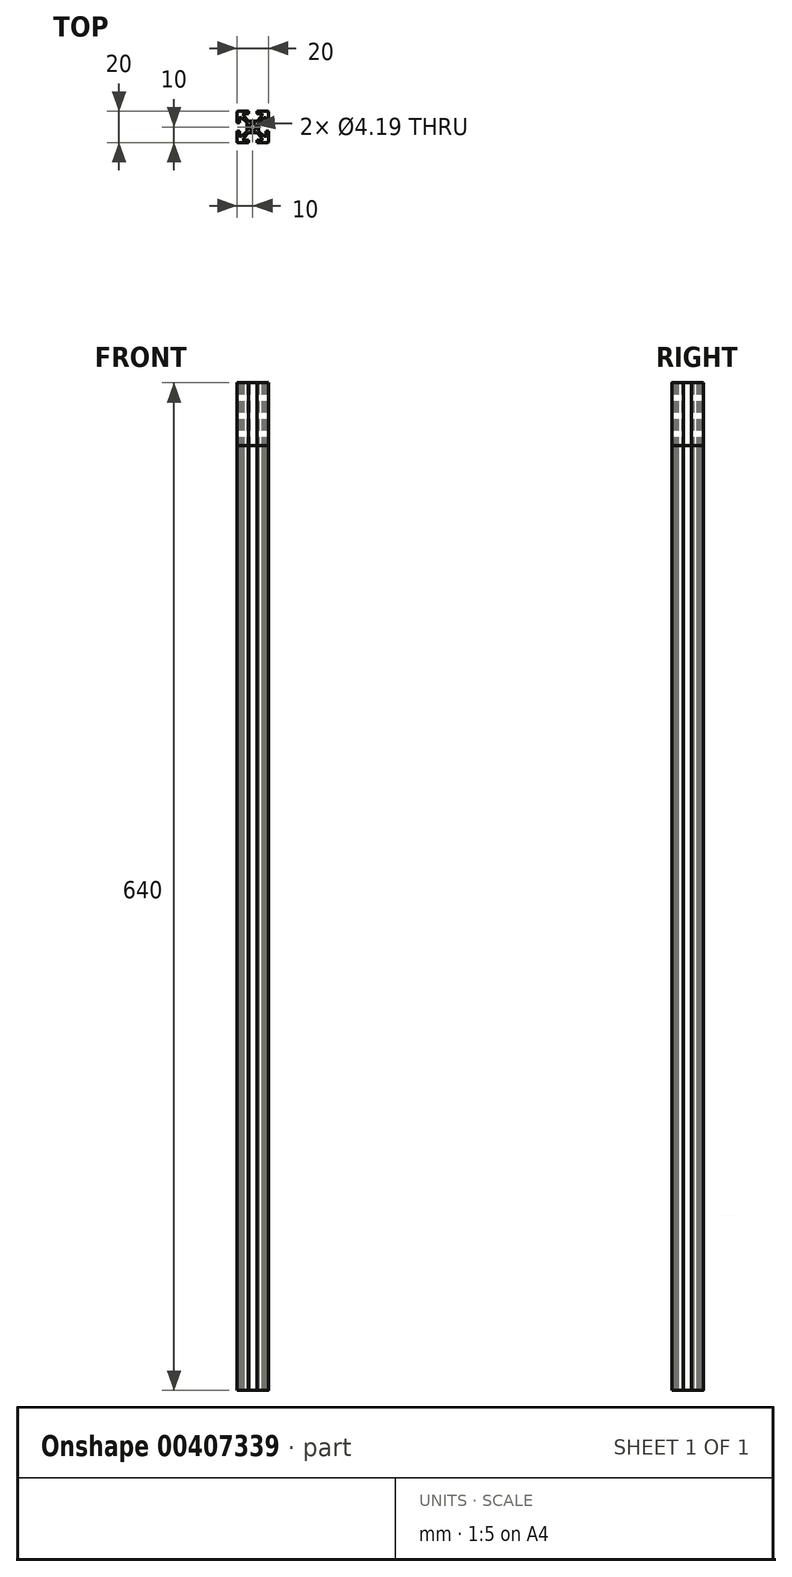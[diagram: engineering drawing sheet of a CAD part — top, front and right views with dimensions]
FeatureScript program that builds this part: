
annotation { "Feature Type Name" : "Feature", "Feature Type Description" : "" }
export const myFeature = defineFeature(function(context is Context, id is Id, definition is map)
    precondition{}
    {
        {
            var Q0;
            Q0=qCreatedBy(makeId("Top.planeOp"),FACE);
            var sketch = newSketch(context, id + "F0", { "sketchPlane" : qUnion([Q0])});
            skLineSegment(sketch, "E0", {"start": v(0, 3.66) * mm, "end": v(2.6, 3.66) * mm});
            skLineSegment(sketch, "E1", {"start": v(2.6, 3.66) * mm, "end": v(6, 7.06) * mm});
            skLineSegment(sketch, "E2", {"start": v(6, 7.06) * mm, "end": v(6, 7.86) * mm});
            skLineSegment(sketch, "E3", {"start": v(5.5, 8.36) * mm, "end": v(3.13, 8.36) * mm});
            skLineSegment(sketch, "E4", {"start": v(2.63, 8.86) * mm, "end": v(2.63, 9.5) * mm});
            skLineSegment(sketch, "E5", {"start": v(3.13, 10) * mm, "end": v(9.5, 10) * mm});
            skLineSegment(sketch, "E6", {"start": v(10, 9.5) * mm, "end": v(10, 3.13) * mm});
            skLineSegment(sketch, "E7", {"start": v(9.5, 2.63) * mm, "end": v(8.86, 2.63) * mm});
            skLineSegment(sketch, "E8", {"start": v(8.36, 3.13) * mm, "end": v(8.36, 5.5) * mm});
            skLineSegment(sketch, "E9", {"start": v(7.86, 6) * mm, "end": v(7.06, 6) * mm});
            skLineSegment(sketch, "E10", {"start": v(7.06, 6) * mm, "end": v(3.66, 2.6) * mm});
            skLineSegment(sketch, "E11", {"start": v(3.66, 2.6) * mm, "end": v(3.66, 0) * mm});
            skArc(sketch, "E12", {"start": v(2.1, 0) * mm, "mid": v(1.48, 1.48) * mm, "end": v(0, 2.1) * mm});
            skPoint(sketch, "E13.visualSharp", {"position": v(2.63, 10) * mm});
            skArc(sketch, "E13.filletArc", {"start": v(3.13, 10) * mm, "mid": v(2.78, 9.85) * mm, "end": v(2.63, 9.5) * mm});
            skPoint(sketch, "E14.visualSharp", {"position": v(2.63, 8.36) * mm});
            skArc(sketch, "E14.filletArc", {"start": v(2.63, 8.86) * mm, "mid": v(2.78, 8.5) * mm, "end": v(3.13, 8.36) * mm});
            skPoint(sketch, "E15.visualSharp", {"position": v(10, 10) * mm});
            skArc(sketch, "E15.filletArc", {"start": v(10, 9.5) * mm, "mid": v(9.85, 9.85) * mm, "end": v(9.5, 10) * mm});
            skPoint(sketch, "E16.visualSharp", {"position": v(10, 2.63) * mm});
            skArc(sketch, "E16.filletArc", {"start": v(9.5, 2.63) * mm, "mid": v(9.85, 2.78) * mm, "end": v(10, 3.13) * mm});
            skPoint(sketch, "E17.visualSharp", {"position": v(8.36, 6) * mm});
            skArc(sketch, "E17.filletArc", {"start": v(8.36, 5.5) * mm, "mid": v(8.21, 5.85) * mm, "end": v(7.86, 6) * mm});
            skPoint(sketch, "E18.visualSharp", {"position": v(8.36, 2.63) * mm});
            skArc(sketch, "E18.filletArc", {"start": v(8.36, 3.13) * mm, "mid": v(8.5, 2.78) * mm, "end": v(8.86, 2.63) * mm});
            skPoint(sketch, "E19.visualSharp", {"position": v(6, 8.36) * mm});
            skArc(sketch, "E19.filletArc", {"start": v(6, 7.86) * mm, "mid": v(5.85, 8.21) * mm, "end": v(5.5, 8.36) * mm});
            skLineSegment(sketch, "E20.MirrorCS", {"start": v(-2.63, 8.86) * mm, "end": v(-2.63, 9.5) * mm});
            skArc(sketch, "E21.MirrorCS", {"start": v(-8.36, 3.13) * mm, "mid": v(-8.5, 2.78) * mm, "end": v(-8.86, 2.63) * mm});
            skArc(sketch, "E22.MirrorCS", {"start": v(-6, 7.86) * mm, "mid": v(-5.85, 8.21) * mm, "end": v(-5.5, 8.36) * mm});
            skArc(sketch, "E23.MirrorCS", {"start": v(-3.13, 10) * mm, "mid": v(-2.78, 9.85) * mm, "end": v(-2.63, 9.5) * mm});
            skArc(sketch, "E24.MirrorCS", {"start": v(-2.63, 8.86) * mm, "mid": v(-2.78, 8.5) * mm, "end": v(-3.13, 8.36) * mm});
            skArc(sketch, "E25.MirrorCS", {"start": v(-10, 9.5) * mm, "mid": v(-9.85, 9.85) * mm, "end": v(-9.5, 10) * mm});
            skLineSegment(sketch, "E26.MirrorCS", {"start": v(-6, 7.06) * mm, "end": v(-6, 7.86) * mm});
            skLineSegment(sketch, "E27.MirrorCS", {"start": v(-9.5, 2.63) * mm, "end": v(-8.86, 2.63) * mm});
            skLineSegment(sketch, "E28.MirrorCS", {"start": v(-7.86, 6) * mm, "end": v(-7.06, 6) * mm});
            skArc(sketch, "E29.MirrorCS", {"start": v(-9.5, 2.63) * mm, "mid": v(-9.85, 2.78) * mm, "end": v(-10, 3.13) * mm});
            skArc(sketch, "E30.MirrorCS", {"start": v(-8.36, 5.5) * mm, "mid": v(-8.21, 5.85) * mm, "end": v(-7.86, 6) * mm});
            skPoint(sketch, "E31.MirrorP", {"position": v(-8.36, 2.63) * mm});
            skPoint(sketch, "E32.MirrorP", {"position": v(-10, 10) * mm});
            skPoint(sketch, "E33.MirrorP", {"position": v(-2.63, 8.36) * mm});
            skPoint(sketch, "E34.MirrorP", {"position": v(-6, 8.36) * mm});
            skPoint(sketch, "E35.MirrorP", {"position": v(-10, 2.63) * mm});
            skLineSegment(sketch, "E36.MirrorCS", {"start": v(0, 3.66) * mm, "end": v(-2.6, 3.66) * mm});
            skLineSegment(sketch, "E37.MirrorCS", {"start": v(-2.6, 3.66) * mm, "end": v(-6, 7.06) * mm});
            skLineSegment(sketch, "E38.MirrorCS", {"start": v(-5.5, 8.36) * mm, "end": v(-3.13, 8.36) * mm});
            skLineSegment(sketch, "E39.MirrorCS", {"start": v(-3.13, 10) * mm, "end": v(-9.5, 10) * mm});
            skLineSegment(sketch, "E40.MirrorCS", {"start": v(-10, 9.5) * mm, "end": v(-10, 3.13) * mm});
            skLineSegment(sketch, "E41.MirrorCS", {"start": v(-8.36, 3.13) * mm, "end": v(-8.36, 5.5) * mm});
            skLineSegment(sketch, "E42.MirrorCS", {"start": v(-3.66, 2.6) * mm, "end": v(-3.66, 0) * mm});
            skLineSegment(sketch, "E43.MirrorCS", {"start": v(-7.06, 6) * mm, "end": v(-3.66, 2.6) * mm});
            skArc(sketch, "E44.MirrorCS", {"start": v(-2.1, 0) * mm, "mid": v(-1.48, 1.48) * mm, "end": v(0, 2.1) * mm});
            skPoint(sketch, "E45.MirrorP", {"position": v(-8.36, 6) * mm});
            skPoint(sketch, "E46.MirrorP", {"position": v(-2.63, 10) * mm});
            skLineSegment(sketch, "E47.MirrorCS", {"start": v(2.63, -8.86) * mm, "end": v(2.63, -9.5) * mm});
            skArc(sketch, "E48.MirrorCS", {"start": v(9.5, -2.63) * mm, "mid": v(9.85, -2.78) * mm, "end": v(10, -3.13) * mm});
            skArc(sketch, "E49.MirrorCS", {"start": v(-9.5, -2.63) * mm, "mid": v(-9.85, -2.78) * mm, "end": v(-10, -3.13) * mm});
            skLineSegment(sketch, "E50.MirrorCS", {"start": v(7.86, -6) * mm, "end": v(7.06, -6) * mm});
            skArc(sketch, "E51.MirrorCS", {"start": v(3.13, -10) * mm, "mid": v(2.78, -9.85) * mm, "end": v(2.63, -9.5) * mm});
            skArc(sketch, "E52.MirrorCS", {"start": v(6, -7.86) * mm, "mid": v(5.85, -8.21) * mm, "end": v(5.5, -8.36) * mm});
            skLineSegment(sketch, "E53.MirrorCS", {"start": v(-6, -7.06) * mm, "end": v(-6, -7.86) * mm});
            skLineSegment(sketch, "E54.MirrorCS", {"start": v(-2.63, -8.86) * mm, "end": v(-2.63, -9.5) * mm});
            skArc(sketch, "E55.MirrorCS", {"start": v(-3.13, -10) * mm, "mid": v(-2.78, -9.85) * mm, "end": v(-2.63, -9.5) * mm});
            skLineSegment(sketch, "E56.MirrorCS", {"start": v(-9.5, -2.63) * mm, "end": v(-8.86, -2.63) * mm});
            skLineSegment(sketch, "E57.MirrorCS", {"start": v(9.5, -2.63) * mm, "end": v(8.86, -2.63) * mm});
            skLineSegment(sketch, "E58.MirrorCS", {"start": v(6, -7.06) * mm, "end": v(6, -7.86) * mm});
            skArc(sketch, "E59.MirrorCS", {"start": v(10, -9.5) * mm, "mid": v(9.85, -9.85) * mm, "end": v(9.5, -10) * mm});
            skArc(sketch, "E60.MirrorCS", {"start": v(2.63, -8.86) * mm, "mid": v(2.78, -8.5) * mm, "end": v(3.13, -8.36) * mm});
            skLineSegment(sketch, "E61.MirrorCS", {"start": v(-7.86, -6) * mm, "end": v(-7.06, -6) * mm});
            skArc(sketch, "E62.MirrorCS", {"start": v(8.36, -3.13) * mm, "mid": v(8.5, -2.78) * mm, "end": v(8.86, -2.63) * mm});
            skArc(sketch, "E63.MirrorCS", {"start": v(-6, -7.86) * mm, "mid": v(-5.85, -8.21) * mm, "end": v(-5.5, -8.36) * mm});
            skArc(sketch, "E64.MirrorCS", {"start": v(-10, -9.5) * mm, "mid": v(-9.85, -9.85) * mm, "end": v(-9.5, -10) * mm});
            skArc(sketch, "E65.MirrorCS", {"start": v(-8.36, -3.13) * mm, "mid": v(-8.5, -2.78) * mm, "end": v(-8.86, -2.63) * mm});
            skArc(sketch, "E66.MirrorCS", {"start": v(-2.63, -8.86) * mm, "mid": v(-2.78, -8.5) * mm, "end": v(-3.13, -8.36) * mm});
            skArc(sketch, "E67.MirrorCS", {"start": v(8.36, -5.5) * mm, "mid": v(8.21, -5.85) * mm, "end": v(7.86, -6) * mm});
            skArc(sketch, "E68.MirrorCS", {"start": v(-8.36, -5.5) * mm, "mid": v(-8.21, -5.85) * mm, "end": v(-7.86, -6) * mm});
            skLineSegment(sketch, "E69.MirrorCS", {"start": v(-8.36, -3.13) * mm, "end": v(-8.36, -5.5) * mm});
            skPoint(sketch, "E70.MirrorP", {"position": v(8.36, -2.63) * mm});
            skLineSegment(sketch, "E71.MirrorCS", {"start": v(7.06, -6) * mm, "end": v(3.66, -2.6) * mm});
            skLineSegment(sketch, "E72.MirrorCS", {"start": v(8.36, -3.13) * mm, "end": v(8.36, -5.5) * mm});
            skLineSegment(sketch, "E73.MirrorCS", {"start": v(2.6, -3.66) * mm, "end": v(6, -7.06) * mm});
            skLineSegment(sketch, "E74.MirrorCS", {"start": v(0, -3.66) * mm, "end": v(2.6, -3.66) * mm});
            skPoint(sketch, "E75.MirrorP", {"position": v(-10, -2.63) * mm});
            skArc(sketch, "E76.MirrorCS", {"start": v(-2.1, 0) * mm, "mid": v(-1.48, -1.48) * mm, "end": v(0, -2.1) * mm});
            skArc(sketch, "E77.MirrorCS", {"start": v(2.1, 0) * mm, "mid": v(1.48, -1.48) * mm, "end": v(0, -2.1) * mm});
            skLineSegment(sketch, "E78.MirrorCS", {"start": v(3.66, -2.6) * mm, "end": v(3.66, 0) * mm});
            skLineSegment(sketch, "E79.MirrorCS", {"start": v(10, -9.5) * mm, "end": v(10, -3.13) * mm});
            skLineSegment(sketch, "E80.MirrorCS", {"start": v(3.13, -10) * mm, "end": v(9.5, -10) * mm});
            skLineSegment(sketch, "E81.MirrorCS", {"start": v(5.5, -8.36) * mm, "end": v(3.13, -8.36) * mm});
            skPoint(sketch, "E82.MirrorP", {"position": v(6, -8.36) * mm});
            skPoint(sketch, "E83.MirrorP", {"position": v(-2.63, -10) * mm});
            skLineSegment(sketch, "E84.MirrorCS", {"start": v(-10, -9.5) * mm, "end": v(-10, -3.13) * mm});
            skPoint(sketch, "E85.MirrorP", {"position": v(2.63, -8.36) * mm});
            skPoint(sketch, "E86.MirrorP", {"position": v(-10, -10) * mm});
            skPoint(sketch, "E87.MirrorP", {"position": v(10, -2.63) * mm});
            skLineSegment(sketch, "E88.MirrorCS", {"start": v(-2.6, -3.66) * mm, "end": v(-6, -7.06) * mm});
            skPoint(sketch, "E89.MirrorP", {"position": v(10, -10) * mm});
            skPoint(sketch, "E90.MirrorP", {"position": v(2.63, -10) * mm});
            skLineSegment(sketch, "E91.MirrorCS", {"start": v(-3.13, -10) * mm, "end": v(-9.5, -10) * mm});
            skPoint(sketch, "E92.MirrorP", {"position": v(-6, -8.36) * mm});
            skPoint(sketch, "E93.MirrorP", {"position": v(8.36, -6) * mm});
            skLineSegment(sketch, "E94.MirrorCS", {"start": v(0, -3.66) * mm, "end": v(-2.6, -3.66) * mm});
            skLineSegment(sketch, "E95.MirrorCS", {"start": v(-7.06, -6) * mm, "end": v(-3.66, -2.6) * mm});
            skPoint(sketch, "E96.MirrorP", {"position": v(-2.63, -8.36) * mm});
            skLineSegment(sketch, "E97.MirrorCS", {"start": v(-3.66, -2.6) * mm, "end": v(-3.66, 0) * mm});
            skLineSegment(sketch, "E98.MirrorCS", {"start": v(-5.5, -8.36) * mm, "end": v(-3.13, -8.36) * mm});
            skPoint(sketch, "E99.MirrorP", {"position": v(-8.36, -6) * mm});
            skPoint(sketch, "E100.MirrorP", {"position": v(-8.36, -2.63) * mm});
            skSolve(sketch);
        }
        {
            var Q0;
            Q0 = qSketchRegion(id + "F0", true);
            extrude(context, id + "F1", {"entities" : qUnion([Q0]), "depth" : 640 * mm});
        }
        {
            var Q0;
            Q0 = qSketchRegion(id + "F0", true);
            extrude(context, id + "F2", {"entities" : qUnion([Q0]), "depth" : 600 * mm});
        }
    });
